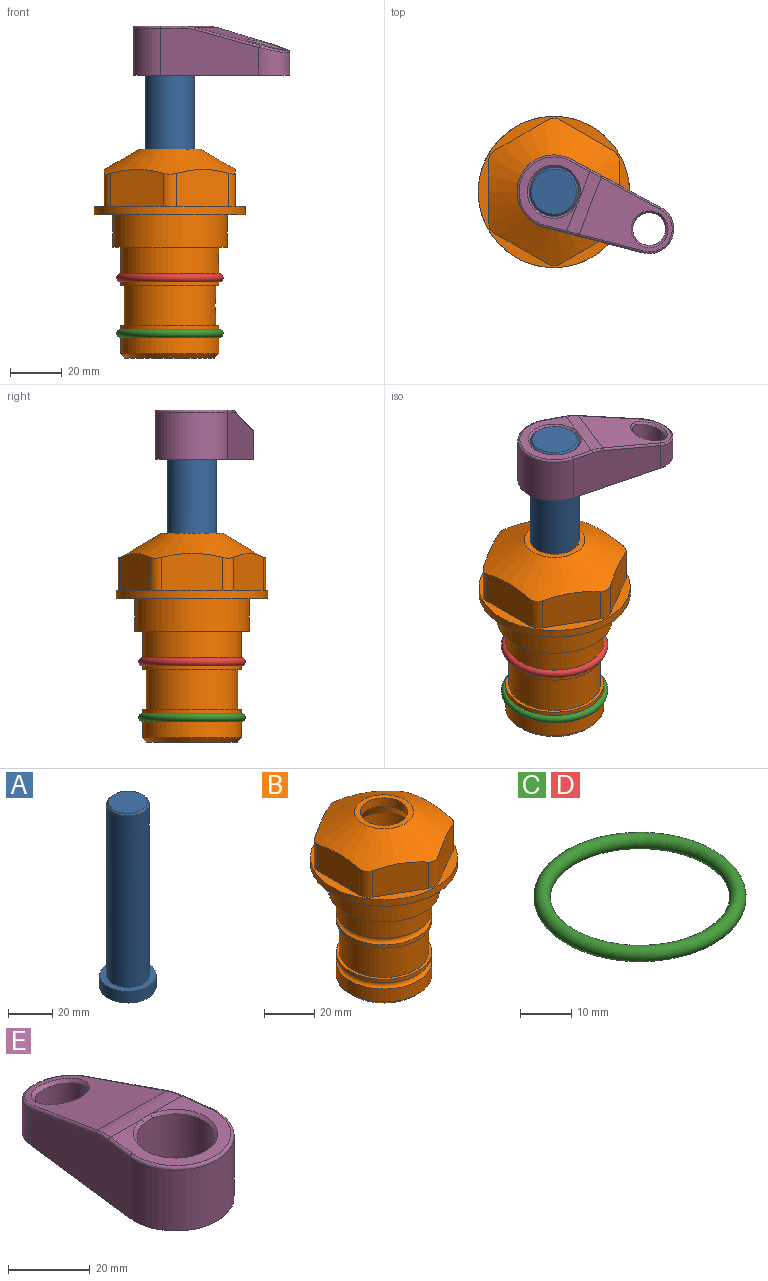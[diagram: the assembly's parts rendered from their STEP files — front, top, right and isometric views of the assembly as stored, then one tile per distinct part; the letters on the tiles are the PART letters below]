
ASSEMBLY  parts=5 mates=4
PART A: 6 faces, bbox 25.4x25.4x101.6 mm
  f0: plane 17.46x17.46mm, normal (0,0,1), area 239.5mm2, adj f5
  f1: plane 25.4x25.4mm, normal (0,0,-1), area 506.7mm2, adj f2
  f2: cylinder r=12.7mm len=25.4mm, axis (0,0,1), area 506.7mm2, adj f1,f3
  f3: plane 25.4x25.4mm, normal (0,0,1), area 221.7mm2, adj f2,f4
  f4: cylinder r=9.53mm len=94.46mm, axis (0,0,1), area 5653mm2, adj f3,f5
  f5: cone r=8.73mm half-angle=45deg, axis (0,0,-1), area 64.4mm2, adj f0,f4
PART B: 36 faces, bbox 58.7x58.7x81 mm
  f0: cylinder r=17.78mm len=35.56mm, axis (0,0,1), area 1670.8mm2, adj f23,f24,f31
  f1: cylinder r=19.05mm len=38.1mm, axis (0,0,1), area 1191.9mm2, adj f26,f27,f30
  f2: plane 58.66x58.66mm, normal (0,0,-1), area 1150.6mm2, adj f3,f28
  f3: cylinder r=29.33mm len=58.66mm, axis (0,0,-1), area 585.1mm2, adj f2,f4
  f4: plane 58.66x58.66mm, normal (0,0,1), area 475.9mm2, adj f3,f5,f6,f7,f8,f9,f10,f11
  f5: plane 20.32x14.34mm, normal (-0.5,0.87,0), area 324.4mm2, adj f4,f15,f16,f17
  f6: plane 20.32x14.34mm, normal (0.5,0.87,0), area 324.4mm2, adj f4,f14,f15,f17
  f7: plane 23.48x14.34mm, normal (1,0,0), area 324.4mm2, adj f4,f13,f14,f17
  f8: plane 20.32x14.34mm, normal (0.5,-0.87,0), area 324.4mm2, adj f4,f12,f13,f17
  f9: plane 20.32x14.34mm, normal (-0.5,-0.87,0), area 324.4mm2, adj f4,f11,f12,f17
  f10: plane 23.48x14.34mm, normal (-1,0,0), area 324.4mm2, adj f4,f11,f16,f17
  f11: cylinder r=5.08mm len=12.85mm, axis (0,0,-1), area 67.2mm2, adj f4,f9,f10,f17
  f12: cylinder r=5.08mm len=12.85mm, axis (0,0,-1), area 67.2mm2, adj f4,f8,f9,f17
  f13: cylinder r=5.08mm len=12.85mm, axis (0,0,-1), area 67.2mm2, adj f4,f7,f8,f17
  f14: cylinder r=5.08mm len=12.85mm, axis (0,0,-1), area 67.2mm2, adj f4,f6,f7,f17
  f15: cylinder r=5.08mm len=12.85mm, axis (0,0,-1), area 67.2mm2, adj f4,f5,f6,f17
  f16: cylinder r=5.08mm len=12.85mm, axis (0,0,-1), area 67.2mm2, adj f4,f5,f10,f17
  f17: cone r=11.73mm half-angle=60deg, axis (0,0,-1), area 2071.8mm2, adj f5,f6,f7,f8,f9,f10,f11,f12
  f18: plane 23.46x23.46mm, normal (0,0,1), area 147.4mm2, adj f17,f35
  f19: plane 34.93x34.93mm, normal (0,0,-1), area 958mm2, adj f29
  f20: cylinder r=19.05mm len=38.1mm, axis (0,0,1), area 760.1mm2, adj f21,f29
  f21: torus R=19.05mm, axis (0,0,1), area 565.3mm2, adj f20,f22
  f22: cylinder r=19.05mm len=38.1mm, axis (0,0,1), area 190mm2, adj f21,f23
  f23: plane 38.1x38.1mm, normal (0,0,1), area 146.9mm2, adj f0,f22
  f24: plane 38.1x38.1mm, normal (0,0,-1), area 146.9mm2, adj f0,f25
  f25: cylinder r=19.05mm len=38.1mm, axis (0,0,1), area 190mm2, adj f24,f26
  f26: torus R=19.05mm, axis (0,0,1), area 565.3mm2, adj f1,f25
  f27: plane 44.45x44.45mm, normal (0,0,-1), area 411.7mm2, adj f1,f28
  f28: cylinder r=22.23mm len=44.45mm, axis (0,0,1), area 1773.5mm2, adj f2,f27
  f29: cone r=19.05mm half-angle=45deg, axis (0,0,1), area 257.5mm2, adj f19,f20
  f30: cylinder r=3.17mm len=6.75mm, axis (-1,0,0), area 128mm2, adj f1,f33
  f31: cylinder r=3.17mm len=6.35mm, axis (-1,0,0), area 102.5mm2, adj f0,f33
  f32: plane 25.4x25.4mm, normal (0,0,1), area 506.7mm2, adj f33
  f33: cylinder r=12.7mm len=66.42mm, axis (0,0,-1), area 5236.2mm2, adj f30,f31,f32,f34
  f34: cone r=9.53mm half-angle=30deg, axis (0,0,-1), area 443.4mm2, adj f33,f35
  f35: cylinder r=9.53mm len=19.05mm, axis (0,0,-1), area 240.9mm2, adj f18,f34
PART C: 1 faces, bbox 44.7x44.7x3.2 mm
  f0: torus R=19.05mm, axis (0,0,1), area 1193.9mm2
PART D: same geometry as C
PART E: 31 faces, bbox 31.7x65.5x19.8 mm
  f0: plane 39.12x18.26mm, normal (0.99,0.12,0), area 612.2mm2, adj f1,f4,f7,f11,f13,f15
  f1: cylinder r=9.53mm len=18.91mm, axis (0,0,-1), area 296.1mm2, adj f0,f2,f7,f17
  f2: plane 39.12x18.26mm, normal (-0.99,0.12,0), area 612.2mm2, adj f1,f4,f7,f12,f14,f16
  f3: cylinder r=6.35mm len=12.7mm, axis (0,0,-1), area 362.4mm2, adj f7,f18
  f4: cylinder r=14.29mm len=28.58mm, axis (0,0,-1), area 882.2mm2, adj f0,f2,f7,f10
  f5: cylinder r=9.53mm len=19.05mm, axis (0,0,-1), area 1092.6mm2, adj f7,f19,f20
  f6: plane 26.99x23.69mm, normal (0,0,1), area 216.2mm2, adj f9,f10,f11,f12,f19
  f7: plane 63.5x28.58mm, normal (0,0,-1), area 661.8mm2, adj f0,f1,f2,f3,f4,f5,f22,f23
  f8: plane 33.52x23.6mm, normal (0,0.26,0.97), area 486mm2, adj f9,f15,f16,f17,f18
  f9: cylinder r=19.05mm len=24.72mm, axis (1,0,0), area 120.4mm2, adj f6,f8,f13,f14,f20
  f10: torus R=13.49mm, axis (0,0,1), area 59mm2, adj f4,f6,f11,f12
  f11: cylinder r=0.79mm len=8.67mm, axis (0.12,-0.99,0), area 10.8mm2, adj f0,f6,f10,f13
  f12: cylinder r=0.79mm len=8.67mm, axis (0.12,0.99,0), area 10.8mm2, adj f2,f6,f10,f14
  f13: bspline ~4.95x1.42mm, area 6.1mm2, adj f0,f9,f11,f15
  f14: bspline ~4.95x1.42mm, area 6.1mm2, adj f2,f9,f12,f16
  f15: cylinder r=0.79mm len=25.95mm, axis (0.12,-0.96,0.26), area 32.9mm2, adj f0,f8,f13,f17
  f16: cylinder r=0.79mm len=25.95mm, axis (0.12,0.96,-0.26), area 32.9mm2, adj f2,f8,f14,f17
  f17: bspline ~18.91x8.38mm, area 30mm2, adj f1,f8,f15,f16
  f18: bspline ~14.29x14.29mm, area 48.3mm2, adj f3,f8
  f19: cone r=9.53mm half-angle=45deg, axis (0,0,1), area 66.5mm2, adj f5,f6,f20
  f20: bspline ~3.22x0.96mm, area 3.5mm2, adj f5,f9,f19
  f21: plane 2.75x2.72mm, normal (0,0,-1), area 2.9mm2, adj f23,f25,f28
  f22: plane 23.05x15.88mm, normal (-0.99,-0.12,0), area 323.6mm2, adj f7,f25,f26,f27,f28,f29
  f23: plane 23.05x15.88mm, normal (0.99,-0.12,0), area 323.6mm2, adj f7,f21,f25,f27,f28,f30
  f24: cylinder r=9.53mm len=10.69mm, axis (0,0,-1), area 114.7mm2, adj f7,f27,f29,f30
  f25: cylinder r=12.7mm len=20.59mm, axis (0,0,-1), area 381.1mm2, adj f7,f21,f22,f23,f26,f28
  f26: plane 2.75x2.72mm, normal (0,0,-1), area 2.9mm2, adj f22,f25,f28
  f27: plane 19.72x18.37mm, normal (0,-0.26,-0.97), area 291.8mm2, adj f22,f23,f24,f28,f29,f30
  f28: cylinder r=15.88mm len=19.92mm, axis (1,0,0), area 54.8mm2, adj f21,f22,f23,f25,f26,f27
  f29: cylinder r=1.59mm len=11mm, axis (0,0,-1), area 34.7mm2, adj f7,f22,f24,f27
  f30: cylinder r=1.59mm len=11mm, axis (0,0,-1), area 34.7mm2, adj f7,f23,f24,f27
PLACE A rot(axis=(0,0,-1),111.4deg) t=(0,0,9.65)mm
PLACE B at identity fixed
PLACE C t=(0,0,-21.59)mm
PLACE D at identity
PLACE E rot(axis=(0,0,-1),111.4deg) t=(0,0,9.65)mm
MATE fastened C.f0 <-> B.f0  axis (0,0,1) through (0,0,-46.1)mm
MATE fastened E.f4 <-> A.f2  axis (0,0,1) through (0,0,73.15)mm
MATE fastened D.f0 <-> B.f0  axis (0,0,1) through (0,0,-24.51)mm
MATE cylindrical B.f0 <-> A.f2  axis (0,0,-1) through (0,0,21.37)mm
